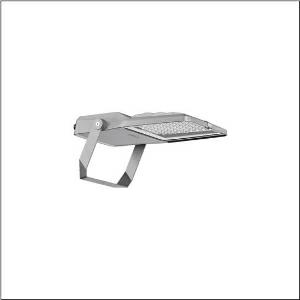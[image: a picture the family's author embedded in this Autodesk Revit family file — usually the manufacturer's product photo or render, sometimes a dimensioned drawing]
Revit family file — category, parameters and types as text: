
# Revit family: floodlight_fl_21_mini___pl64_5xa7776c2e1a_42f0
name_source: partatom
category: Lighting Fixtures
units: mm (PartAtom-declared; Revit-internal decimal feet)

## family parameters
Cut with Voids When Loaded = No
Host = Face
Light Source = No
Part Type = Normal
Room Calculation Point = No
Round Connector Dimension = Use Diameter
Shared = No

## types (1)
- --- (1 x LED, 11770 lm, 89 W, 3000K)
    Apparent Load = 89 VA
    CIE Flux Codes = 28 80 98 100 100
    Color Rendering = 70
    Color Temperature = 3000K
    Default Elevation = 1800 mm
    Description = Floodlight FL 21 mini, floodlight, primary light control with lens, of PMMA, primary optical cover: protective disc, of toughened safety glass, transparent, light distribution: PL64, light emission: direct distribution, installation type: surface-mounted, LED, High Power LED, rated luminous flux: 11.770lm, luminous efficacy: 132lm/W, light colour: 730, colour temperature: 3000K, control gear: Smart Interface (Zhaga), control: flexible luminous flux parameterisation, time-dependent luminous flux control, constant luminous flux control, overheat protection, pre-setting: logarithmic dimming characteristic, with terminal, 6-pole, mains connection: 220..240V, AC, 50/60Hz, start of lifetime: 89W, end of service life: 94W, reduction: 43W, luminaire housing, of diecast aluminium, powder-coated, Siteco® metallic grey (DB 702S), corrosivity category C5 mid according to DIN EN ISO 12944, suitable for swimming pools, chlorine-resistant, sealing non-destructively replaceable, mounting bracket, of steel, galvanised, powder-coated, Siteco® metallic grey (DB 702S), Smart Interface below and above, protection rating (complete): IP66, insulation class (complete): insulation class II (safety insulation), certification: CE, ENEC, VDE, protection symbol: D, impact resistance: IK08, permissible operating ambient temperature: -40..+40°C, permissible operating ambient temperature for outdoor applications: -40..+50°C, standard: DIN EN 12944, LABS conformity tested according to VDMA 24364:2018-05, packaging unit: 1 piece

Light Distribution: PL64
    Height = 70 mm
    Lamp = 1 x LED
    Lamp Light Flux = 11770 lm
    Lamp Power = 89 W
    Lamp count = 1
    Length = 485 mm
    Luminous efficacy = 132 lm/W
    Manufacturer = Siteco
    ModVariant = No
    Model = 5XA7776C2E1A
    Number of Poles = 1
    OnlyDefault = Yes
    Power Factor = 1
    Product Name = Floodlight FL 21 mini | PL64
    Product group = floodlight | pylon annexe
    ProductGroupID = 6200
    Protection Class = Protection class II
    Protection Degree = IP 66
    RLX_Detail_Level = 1
    RLX_Emergency_Light_Flux = 0 lm
    RLX_Emergency_Type = 0
    RLX_Emergency_Type_DB = No
    RlxData = <blob elided: 95957 chars, md5=b8c45df8>
    Socket = socket
    Standby Power = 0 W
    System Light Flux = 11770 lm
    System Power = 89 W
    Type Comments = factory setting: luminous flux: 100 % | dim-lin: 254 | 456 mA
    Type Image = l_1006845.jpg
    URL = http://relux.com
    VarID = @adj_165380
    Voltage = 0 V
    Weight = 0.00 kg
    Width = 337 mm

## geometry (parser evidence)
native form markers: Blend x4, Sweep x11
no freeform markers — native parametric forms only
